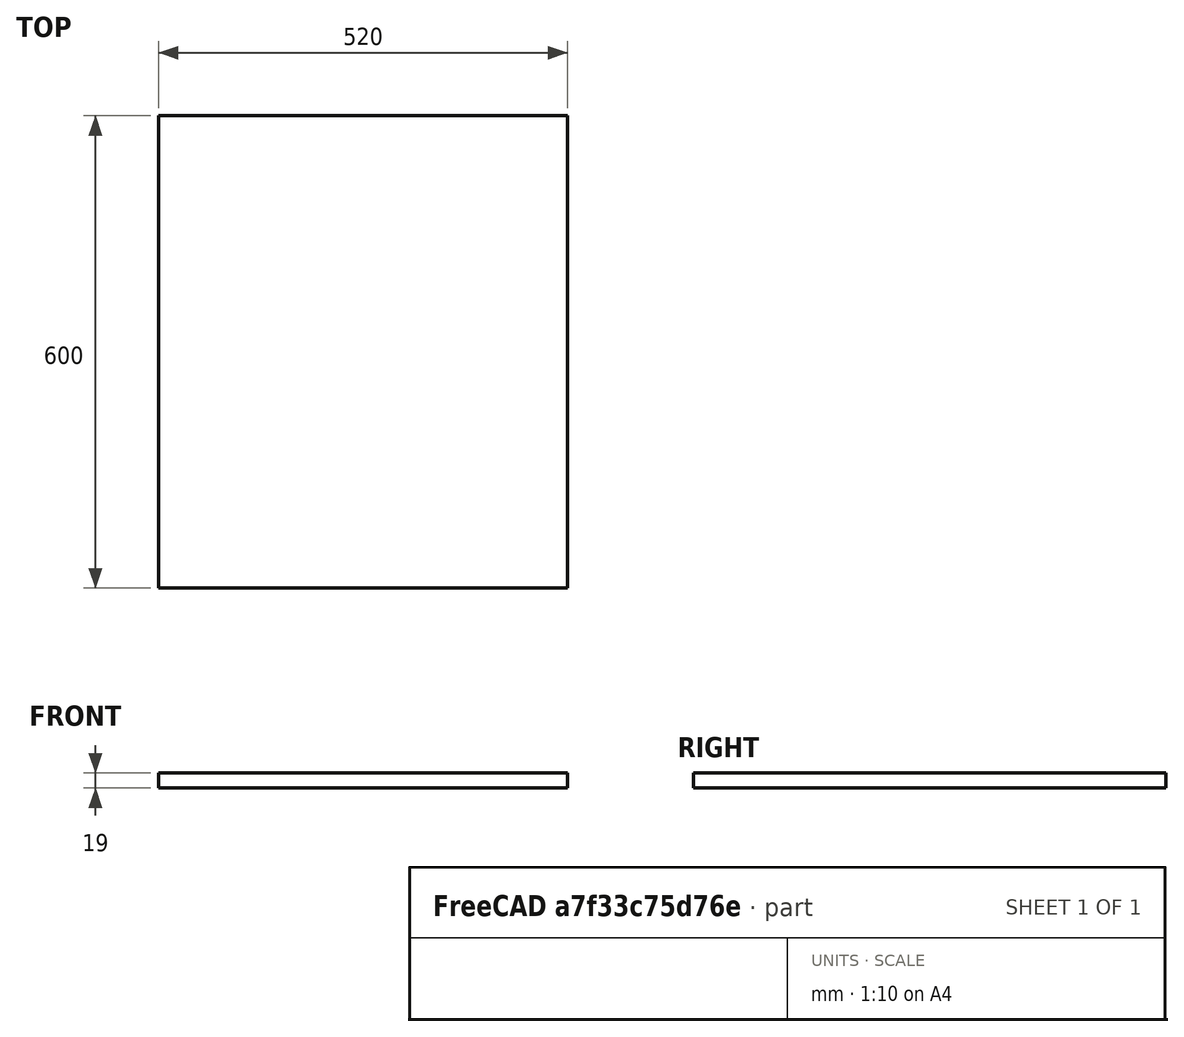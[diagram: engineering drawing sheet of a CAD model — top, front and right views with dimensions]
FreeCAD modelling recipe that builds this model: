
FCSTD DOCUMENT  (FreeCAD 1.0RUnknown)
Label: wardrobe_base_corpus03_jan
License: All rights reserved
LicenseURL: https://en.wikipedia.org/wiki/All_rights_reserved
objects: PartDesign::CoordinateSystem×9, Sketcher::SketchObject×2, PartDesign::Pad×1, PartDesign::Body×1, App::Part×1
note: 17 computed .brp shape members not serialized (recipe doc carries the construction recipe); baked Part::Feature solids carry a one-line shape summary decoded from their .brp
EXTERNAL_REF file=../../mastersketch.FCStd obj=Sketch001
EXTERNAL_REF file=../../mastersketch.FCStd obj=Spreadsheet

FEATURE [Sketcher::SketchObject] Sketch
  ArcFitTolerance = 1e-06
  AttachmentSupport = -> [XY_Plane]
  FullyConstrained = true
  MakeInternals = false
  MapMode = 5
  expr: Constraints[10] = mastersketch#<<corpus>>.Constraints.corpus03_width
  expr: Constraints[11] = mastersketch#Spreadsheet.corpus_depth
  sketch-geometry (5):
    g0: LineSegment StartX=-260 StartY=-300 StartZ=0 EndX=260 EndY=-300 EndZ=0
    g1: LineSegment StartX=260 StartY=-300 StartZ=0 EndX=260 EndY=300 EndZ=0
    g2: LineSegment StartX=260 StartY=300 StartZ=0 EndX=-260 EndY=300 EndZ=0
    g3: LineSegment StartX=-260 StartY=300 StartZ=0 EndX=-260 EndY=-300 EndZ=0
    g4: GeomPoint [constr] X=0 Y=0 Z=0
  constraints (12):
    c: Coincident(g0,g1)
    c: Coincident(g1,g2)
    c: Coincident(g2,g3)
    c: Coincident(g3,g0)
    c: Horizontal(g0)
    c: Horizontal(g2)
    c: Vertical(g1)
    c: Vertical(g3)
    c: Symmetric(g2,g0,g4)
    c: Coincident(g4,g-1)
    c: DistanceX(g0,g0) = 520
    c: DistanceY(g3,g3) = 600
FEATURE [PartDesign::Pad] Pad
  Direction = (0,0,1)
  Length = 19
  Length2 = 10
  Profile = -> Sketch
  ReferenceAxis = -> Sketch [N_Axis]
  Refine = true
  Suppressed = false
  Type = 0
  expr: Length = mastersketch#Spreadsheet.corpus_outer_thickness
FEATURE [PartDesign::CoordinateSystem] LCS_1  label="LCS_left"
  AttacherType = Attacher::AttachEngine3D
  AttachmentSupport = -> [Pad]
  MapMode = 45
  Placement = pos=(-260,1.42e-14,19) rot=(0,0.707107,0.707107;3.14159rad)
FEATURE [PartDesign::CoordinateSystem] LCS_right  label="LCS-right"
  AttacherType = Attacher::AttachEngine3D
  AttachmentSupport = -> [Pad]
  MapMode = 45
  Placement = pos=(260,-1.42e-14,19) rot=(0,0.707107,0.707107;3.14159rad)
FEATURE [Sketcher::SketchObject] Sketch_1  label="feet_placement"
  ArcFitTolerance = 1e-06
  AttachmentSupport = -> [Pad]
  FullyConstrained = true
  MakeInternals = false
  MapMode = 5
  Placement = pos=(0,0,0) rot=(1,0,0;3.14159rad)
  expr: Constraints[10] = mastersketch#Spreadsheet.corpus_width - 100
  expr: Constraints[11] = mastersketch#Spreadsheet.corpus_depth - 140
  sketch-geometry (5):
    g0: LineSegment StartX=-220 StartY=-230 StartZ=0 EndX=220 EndY=-230 EndZ=0
    g1: LineSegment StartX=220 StartY=-230 StartZ=0 EndX=220 EndY=230 EndZ=0
    g2: LineSegment StartX=220 StartY=230 StartZ=0 EndX=-220 EndY=230 EndZ=0
    g3: LineSegment StartX=-220 StartY=230 StartZ=0 EndX=-220 EndY=-230 EndZ=0
    g4: GeomPoint [constr] X=0 Y=0 Z=0
  constraints (12):
    c: Coincident(g0,g1)
    c: Coincident(g1,g2)
    c: Coincident(g2,g3)
    c: Coincident(g3,g0)
    c: Horizontal(g0)
    c: Horizontal(g2)
    c: Vertical(g1)
    c: Vertical(g3)
    c: Symmetric(g2,g0,g4)
    c: Coincident(g4,g-1)
    c: DistanceX(g0,g0) = 440
    c: DistanceY(g3,g3) = 460
FEATURE [PartDesign::Body] Body  label="wardrobe_base_corpus03_jan"
  AllowCompound = false
  Group = -> [Sketch,Pad,Sketch_1]
  Origin = -> Origin
  Tip = -> Pad
FEATURE [PartDesign::CoordinateSystem] LCS_2  label="LCS_feet0"
  AttacherType = Attacher::AttachEngine3D
  AttachmentSupport = -> [Sketch_1]
  MapMode = 1
  Placement = pos=(-220,-230,0) rot=(0,0,1;0rad)
FEATURE [PartDesign::CoordinateSystem] LCS_feet1
  AttacherType = Attacher::AttachEngine3D
  AttachmentSupport = -> [Sketch_1]
  MapMode = 1
  Placement = pos=(220,-230,0) rot=(0,0,1;0rad)
FEATURE [PartDesign::CoordinateSystem] LCS_feet2
  AttacherType = Attacher::AttachEngine3D
  AttachmentSupport = -> [Sketch_1]
  MapMode = 1
  Placement = pos=(220,230,0) rot=(0,0,1;0rad)
FEATURE [PartDesign::CoordinateSystem] LCS_feet3
  AttacherType = Attacher::AttachEngine3D
  AttachmentSupport = -> [Sketch_1]
  MapMode = 1
  Placement = pos=(-220,230,0) rot=(0,0,1;0rad)
FEATURE [PartDesign::CoordinateSystem] LCS_back
  AttacherType = Attacher::AttachEngine3D
  AttachmentSupport = -> [Pad]
  MapMode = 45
  Placement = pos=(0,300,0) rot=(0.57735,0.57735,0.57735;2.0944rad)
FEATURE [PartDesign::CoordinateSystem] LCS_door
  AttacherType = Attacher::AttachEngine3D
  AttachmentSupport = -> [Pad]
  MapMode = 7
  Placement = pos=(260,-300,0) rot=(0,1,0;3.14159rad)
FEATURE [PartDesign::CoordinateSystem] LCS_Origin
  AttacherType = Attacher::AttachEngine3D
  AttachmentSupport = -> [X_Axis001]
  MapMode = 2
FEATURE [App::Part] wardrobe_base_corpus03_jan  label="wardrobe_base_corpus03_jan001"
  DrawingName = wardrobe_base_corpus03_jan.FCStd
  Group = -> [LCS_Origin,LCS_1,LCS_right,LCS_2,LCS_feet1,LCS_feet2,LCS_feet3,LCS_back,LCS_door,Body]
  Origin = -> Origin001
  PartDescription = wardrobe_base_corpus03_jan
  PartID = wardrobe_base_corpus03_jan
